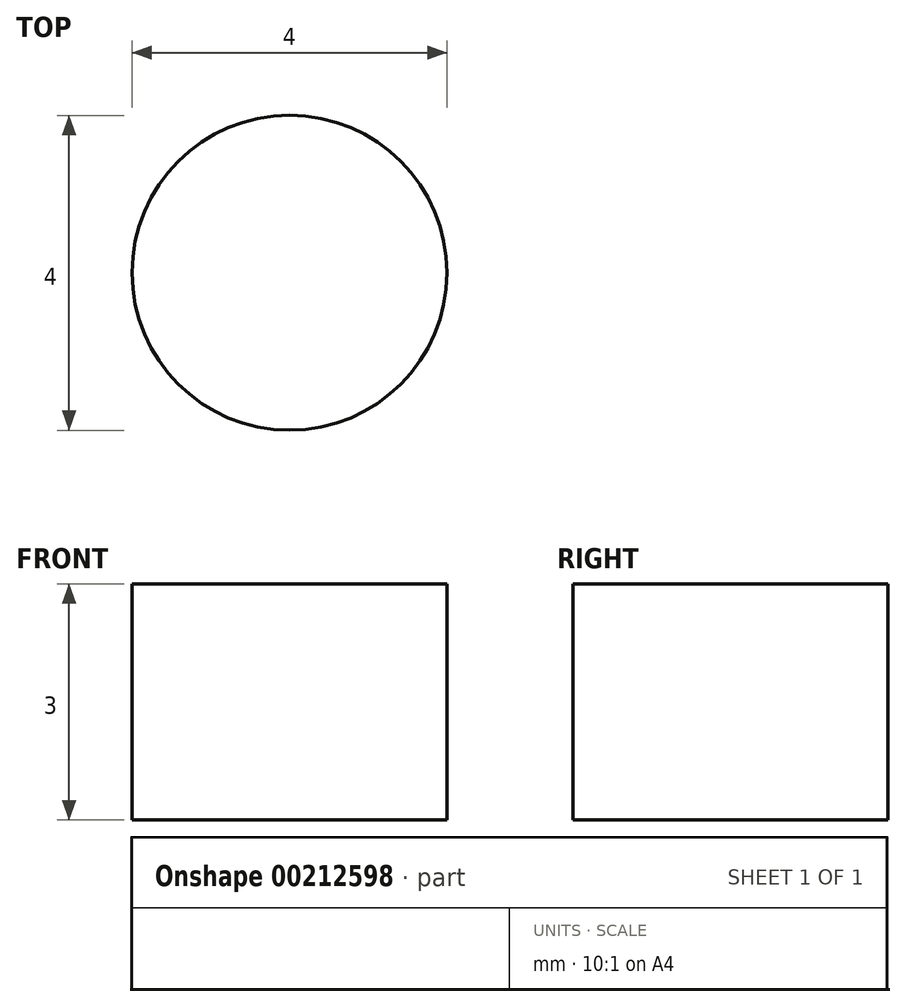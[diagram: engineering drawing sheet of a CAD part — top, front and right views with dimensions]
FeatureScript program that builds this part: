
annotation { "Feature Type Name" : "Feature", "Feature Type Description" : "" }
export const myFeature = defineFeature(function(context is Context, id is Id, definition is map)
    precondition{}
    {
        {
            var Q0;
            Q0=qCreatedBy(makeId("Top.planeOp"),FACE);
            var sketch = newSketch(context, id + "F0", { "sketchPlane" : qUnion([Q0])});
            skCircle(sketch, "E0", {"center": v(43.46, 21.61) * mm, "radius": 2 * mm});
            skCircle(sketch, "E1", {"center": v(0, 23) * mm, "radius": 2 * mm});
            skCircle(sketch, "E2", {"center": v(-43.46, 21.61) * mm, "radius": 2 * mm});
            skCircle(sketch, "E3", {"center": v(-43.46, -21.61) * mm, "radius": 2 * mm});
            skCircle(sketch, "E4", {"center": v(0, -23) * mm, "radius": 2 * mm});
            skCircle(sketch, "E5", {"center": v(43.46, -21.61) * mm, "radius": 2 * mm});
            skLineSegment(sketch, "E6", {"start": v(40, -33) * mm, "end": v(-40, -33) * mm});
            skArc(sketch, "E7", {"start": v(40, -33) * mm, "mid": v(50.6, -28.6) * mm, "end": v(55, -18) * mm});
            skLineSegment(sketch, "E8", {"start": v(55, 18) * mm, "end": v(55, -18) * mm});
            skArc(sketch, "E9", {"start": v(55, 18) * mm, "mid": v(50.6, 28.6) * mm, "end": v(40, 33) * mm});
            skLineSegment(sketch, "E10", {"start": v(40, 33) * mm, "end": v(-40, 33) * mm});
            skArc(sketch, "E11", {"start": v(-40, 33) * mm, "mid": v(-50.6, 28.6) * mm, "end": v(-55, 18) * mm});
            skLineSegment(sketch, "E12", {"start": v(-55, 18) * mm, "end": v(-55, -18) * mm});
            skArc(sketch, "E13", {"start": v(-55, -18) * mm, "mid": v(-50.6, -28.6) * mm, "end": v(-40, -33) * mm});
            skLineSegment(sketch, "E14", {"start": v(-25, 14) * mm, "end": v(25, 14) * mm});
            skArc(sketch, "E15", {"start": v(25, 14) * mm, "mid": v(32.57, 11.28) * mm, "end": v(36, 4) * mm});
            skLineSegment(sketch, "E16", {"start": v(36, 4) * mm, "end": v(36, -2) * mm});
            skLineSegment(sketch, "E17", {"start": v(36, -2) * mm, "end": v(36, 4) * mm});
            skArc(sketch, "E18", {"start": v(36, 4) * mm, "mid": v(32.57, 11.28) * mm, "end": v(25, 14) * mm});
            skLineSegment(sketch, "E19", {"start": v(25, 14) * mm, "end": v(-25, 14) * mm});
            skArc(sketch, "E20", {"start": v(-25, 14) * mm, "mid": v(-32.57, 11.28) * mm, "end": v(-36, 4) * mm});
            skLineSegment(sketch, "E21", {"start": v(-36, 4) * mm, "end": v(-36, -2) * mm});
            skArc(sketch, "E22", {"start": v(-36, -2) * mm, "mid": v(-32.78, -9.78) * mm, "end": v(-25, -13) * mm});
            skLineSegment(sketch, "E23", {"start": v(-25, -13) * mm, "end": v(25, -13) * mm});
            skArc(sketch, "E24", {"start": v(25, -13) * mm, "mid": v(32.78, -9.78) * mm, "end": v(36, -2) * mm});
            skSolve(sketch);
        }
        {
            var Q0;
            Q0=makeQuery(id+"F0.imprint","IMPRINT",FACE,{"disambiguationData":[TD([[makeQuery(id+"F0.imprint","IMPRINT",EDGE,{"derivedFrom":sQuery(id+"F0.wireOp",EDGE,"E0")}),1.0]])]});
            extrude(context, id + "F1", {"entities" : qUnion([Q0]), "depth" : 3 * mm});
        }
    });
